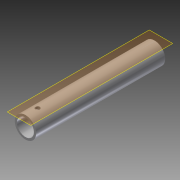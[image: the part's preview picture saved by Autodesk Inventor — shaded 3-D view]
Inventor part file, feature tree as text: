
AUTODESK INVENTOR PART (.ipt)
format: ipt  version: 2013 (Build 170138000, 138)  size: 107,008 bytes
history: native  units: in
note: dims shown in document units (in); Inventor stores cm internally (conversion verified against a paired STEP export)
features: reference x3, extrude x2, sketch x2, plane x1
ambient origin geometry x8: Origin, YZ Plane, XZ Plane, XY Plane, X Axis, Y Axis, Z Axis, Center Point
bodies: Solid1 (feature_tree)
feature tree (8):
  extrude  "Extrusion1"  Depth=1.05in
  plane  "Work Plane1"
  extrude  "Extrusion2"  Depth=1.0in TaperAngle=0.0deg
  sketch  "Sketch1"  dims[d0=1.32in d2=1.05in]
  sketch  "Sketch2"  dims[d3=8.0in d4=0.0in d5=1.0in d6=0.0in]
  reference  "Reference1"
  reference  "Reference2"
  reference  "Reference3"
